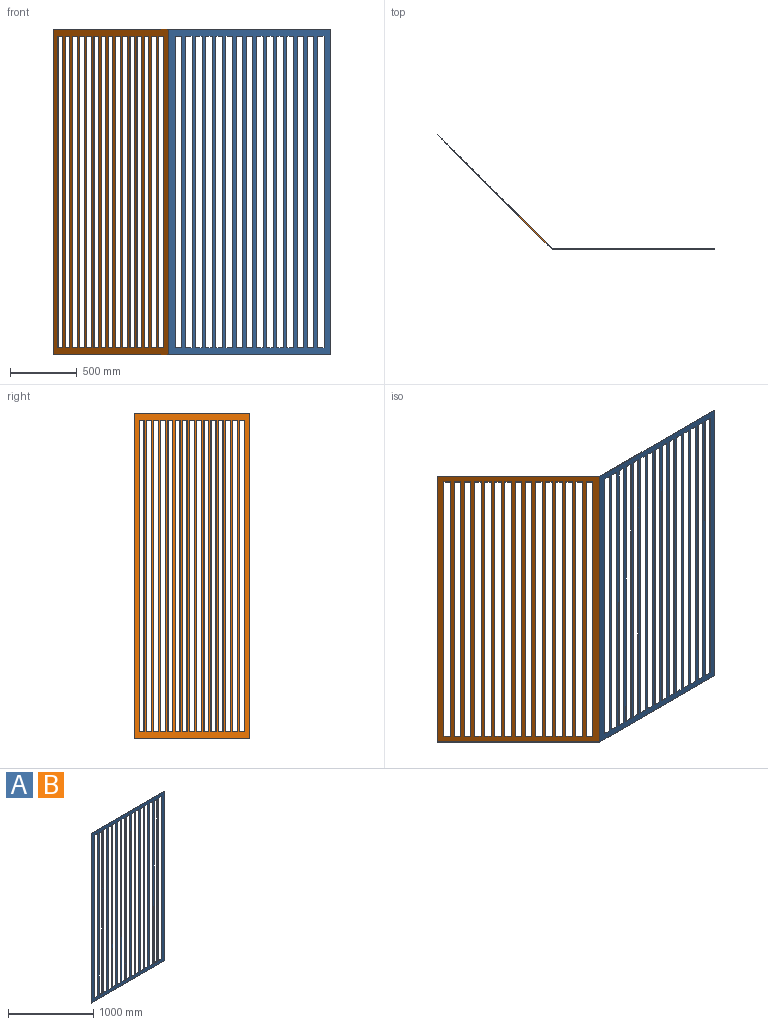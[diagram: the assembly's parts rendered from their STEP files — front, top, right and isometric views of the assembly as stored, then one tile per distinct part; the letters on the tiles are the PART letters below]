
ASSEMBLY  parts=2 mates=1
PART A: 66 faces, bbox 1219.2x3.2x2438.4 mm
  f0: plane 50.8x3.18mm, normal (0,0,-1), area 161.3mm2, adj f1,f63,f64,f65
  f1: plane 2336.8x3.18mm, normal (-1,0,0), area 7419.3mm2, adj f0,f2,f64,f65
  f2: plane 50.8x3.18mm, normal (0,0,1), area 161.3mm2, adj f1,f63,f64,f65
  f3: plane 50.8x3.18mm, normal (0,0,-1), area 161.3mm2, adj f4,f48,f64,f65
  f4: plane 2336.8x3.18mm, normal (-1,0,0), area 7419.3mm2, adj f3,f5,f64,f65
  f5: plane 50.8x3.18mm, normal (0,0,1), area 161.3mm2, adj f4,f48,f64,f65
  f6: plane 50.8x3.18mm, normal (0,0,-1), area 161.3mm2, adj f7,f49,f64,f65
  f7: plane 2336.8x3.18mm, normal (-1,0,0), area 7419.3mm2, adj f6,f8,f64,f65
  f8: plane 50.8x3.18mm, normal (0,0,1), area 161.3mm2, adj f7,f49,f64,f65
  f9: plane 50.8x3.18mm, normal (0,0,-1), area 161.3mm2, adj f10,f50,f64,f65
  f10: plane 2336.8x3.18mm, normal (-1,0,0), area 7419.3mm2, adj f9,f11,f64,f65
  f11: plane 50.8x3.18mm, normal (0,0,1), area 161.3mm2, adj f10,f50,f64,f65
  f12: plane 50.8x3.18mm, normal (0,0,-1), area 161.3mm2, adj f13,f51,f64,f65
  f13: plane 2336.8x3.18mm, normal (-1,0,0), area 7419.3mm2, adj f12,f14,f64,f65
  f14: plane 50.8x3.18mm, normal (0,0,1), area 161.3mm2, adj f13,f51,f64,f65
  f15: plane 50.8x3.18mm, normal (0,0,-1), area 161.3mm2, adj f16,f52,f64,f65
  f16: plane 2336.8x3.18mm, normal (-1,0,0), area 7419.3mm2, adj f15,f17,f64,f65
  f17: plane 50.8x3.18mm, normal (0,0,1), area 161.3mm2, adj f16,f52,f64,f65
  f18: plane 50.8x3.18mm, normal (0,0,-1), area 161.3mm2, adj f19,f53,f64,f65
  f19: plane 2336.8x3.18mm, normal (-1,0,0), area 7419.3mm2, adj f18,f20,f64,f65
  f20: plane 50.8x3.18mm, normal (0,0,1), area 161.3mm2, adj f19,f53,f64,f65
  f21: plane 50.8x3.18mm, normal (0,0,-1), area 161.3mm2, adj f22,f54,f64,f65
  f22: plane 2336.8x3.18mm, normal (-1,0,0), area 7419.3mm2, adj f21,f23,f64,f65
  f23: plane 50.8x3.18mm, normal (0,0,1), area 161.3mm2, adj f22,f54,f64,f65
  f24: plane 50.8x3.18mm, normal (0,0,-1), area 161.3mm2, adj f25,f55,f64,f65
  f25: plane 2336.8x3.18mm, normal (-1,0,0), area 7419.3mm2, adj f24,f26,f64,f65
  f26: plane 50.8x3.18mm, normal (0,0,1), area 161.3mm2, adj f25,f55,f64,f65
  f27: plane 50.8x3.18mm, normal (0,0,-1), area 161.3mm2, adj f28,f56,f64,f65
  f28: plane 2336.8x3.18mm, normal (-1,0,0), area 7419.3mm2, adj f27,f29,f64,f65
  f29: plane 50.8x3.18mm, normal (0,0,1), area 161.3mm2, adj f28,f56,f64,f65
  f30: plane 50.8x3.18mm, normal (0,0,-1), area 161.3mm2, adj f31,f57,f64,f65
  f31: plane 2336.8x3.18mm, normal (-1,0,0), area 7419.3mm2, adj f30,f32,f64,f65
  f32: plane 50.8x3.18mm, normal (0,0,1), area 161.3mm2, adj f31,f57,f64,f65
  f33: plane 50.8x3.18mm, normal (0,0,-1), area 161.3mm2, adj f34,f58,f64,f65
  f34: plane 2336.8x3.18mm, normal (-1,0,0), area 7419.3mm2, adj f33,f35,f64,f65
  f35: plane 50.8x3.18mm, normal (0,0,1), area 161.3mm2, adj f34,f58,f64,f65
  f36: plane 50.8x3.18mm, normal (0,0,-1), area 161.3mm2, adj f37,f59,f64,f65
  f37: plane 2336.8x3.18mm, normal (-1,0,0), area 7419.3mm2, adj f36,f38,f64,f65
  f38: plane 50.8x3.18mm, normal (0,0,1), area 161.3mm2, adj f37,f59,f64,f65
  f39: plane 50.8x3.18mm, normal (0,0,-1), area 161.3mm2, adj f40,f60,f64,f65
  f40: plane 2336.8x3.18mm, normal (-1,0,0), area 7419.3mm2, adj f39,f41,f64,f65
  f41: plane 50.8x3.18mm, normal (0,0,1), area 161.3mm2, adj f40,f60,f64,f65
  f42: plane 2438.4x3.18mm, normal (-1,0,0), area 7741.9mm2, adj f43,f61,f64,f65
  f43: plane 1219.2x3.18mm, normal (0,0,-1), area 3871mm2, adj f42,f44,f64,f65
  f44: plane 2438.4x3.18mm, normal (1,0,0), area 7741.9mm2, adj f43,f61,f64,f65
  f45: plane 50.8x3.18mm, normal (0,0,1), area 161.3mm2, adj f46,f62,f64,f65
  f46: plane 2336.8x3.18mm, normal (1,0,0), area 7419.3mm2, adj f45,f47,f64,f65
  f47: plane 50.8x3.18mm, normal (0,0,-1), area 161.3mm2, adj f46,f62,f64,f65
  f48: plane 2336.8x3.18mm, normal (1,0,0), area 7419.3mm2, adj f3,f5,f64,f65
  f49: plane 2336.8x3.18mm, normal (1,0,0), area 7419.3mm2, adj f6,f8,f64,f65
  f50: plane 2336.8x3.18mm, normal (1,0,0), area 7419.3mm2, adj f9,f11,f64,f65
  f51: plane 2336.8x3.18mm, normal (1,0,0), area 7419.3mm2, adj f12,f14,f64,f65
  f52: plane 2336.8x3.18mm, normal (1,0,0), area 7419.3mm2, adj f15,f17,f64,f65
  f53: plane 2336.8x3.18mm, normal (1,0,0), area 7419.3mm2, adj f18,f20,f64,f65
  f54: plane 2336.8x3.18mm, normal (1,0,0), area 7419.3mm2, adj f21,f23,f64,f65
  f55: plane 2336.8x3.18mm, normal (1,0,0), area 7419.3mm2, adj f24,f26,f64,f65
  f56: plane 2336.8x3.18mm, normal (1,0,0), area 7419.3mm2, adj f27,f29,f64,f65
  f57: plane 2336.8x3.18mm, normal (1,0,0), area 7419.3mm2, adj f30,f32,f64,f65
  f58: plane 2336.8x3.18mm, normal (1,0,0), area 7419.3mm2, adj f33,f35,f64,f65
  f59: plane 2336.8x3.18mm, normal (1,0,0), area 7419.3mm2, adj f36,f38,f64,f65
  f60: plane 2336.8x3.18mm, normal (1,0,0), area 7419.3mm2, adj f39,f41,f64,f65
  f61: plane 1219.2x3.18mm, normal (0,0,1), area 3871mm2, adj f42,f44,f64,f65
  f62: plane 2336.8x3.18mm, normal (-1,0,0), area 7419.3mm2, adj f45,f47,f64,f65
  f63: plane 2336.8x3.18mm, normal (1,0,0), area 7419.3mm2, adj f0,f2,f64,f65
  f64: plane 2438.4x1219.2mm, normal (0,-1,0), area 1192255.7mm2, adj f0,f1,f2,f3,f4,f5,f6,f7
  f65: plane 2438.4x1219.2mm, normal (0,1,0), area 1192255.7mm2, adj f0,f1,f2,f3,f4,f5,f6,f7
PART B: same geometry as A
PLACE A t=(-308.5,-188.02,277.71)mm fixed
PLACE B rot(axis=(0,0,-1),45deg) t=(-1362.61,210.54,277.71)mm
MATE fastened A.f61 <-> B.f61  axis (0,0,-1) through (-964.05,-188.02,1249.91)mm
